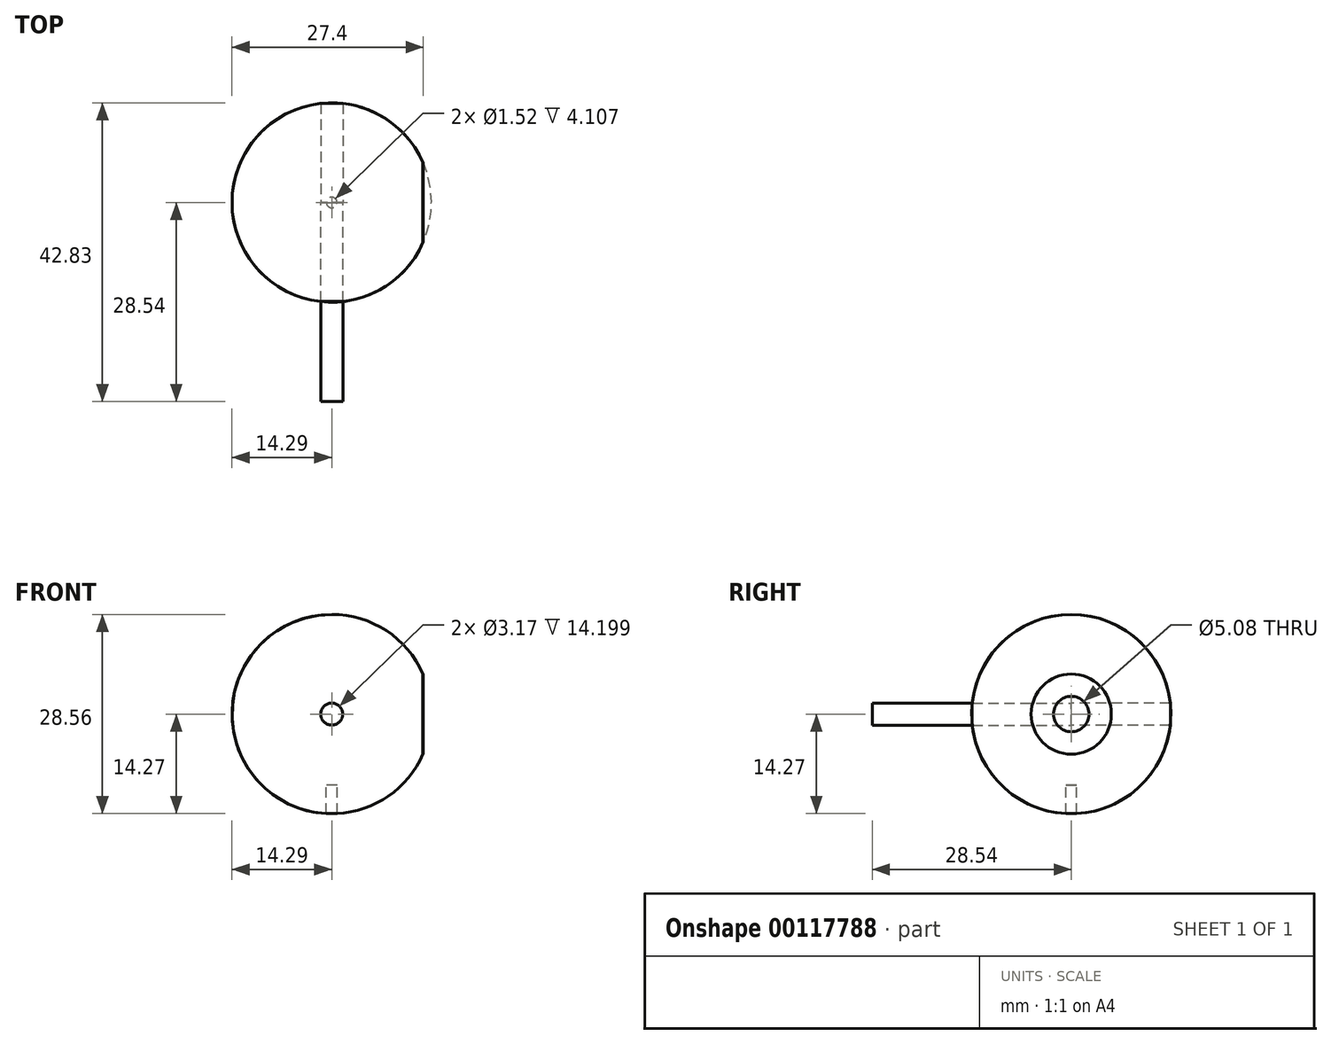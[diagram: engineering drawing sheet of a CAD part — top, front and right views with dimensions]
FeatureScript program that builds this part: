
annotation { "Feature Type Name" : "Feature", "Feature Type Description" : "" }
export const myFeature = defineFeature(function(context is Context, id is Id, definition is map)
    precondition{}
    {
        {
            var Q0;
            Q0=qCreatedBy(makeId("Front.planeOp"),FACE);
            var sketch = newSketch(context, id + "F0", { "sketchPlane" : qUnion([Q0])});
            skCircle(sketch, "E0", {"center": v(0, 0) * mm, "radius": 14.29 * mm});
            skLineSegment(sketch, "E1", {"start": v(0, 14.29) * mm, "end": v(0, -14.29) * mm});
            skSolve(sketch);
        }
        {
            var Q0;
            {var subQ0=sQuery(id+"F0.wireOp",EDGE,"E1");Q0=makeQuery(id+"F0.imprint","IMPRINT",FACE,{"disambiguationData":[TD([[makeQuery(id+"F0.imprint","IMPRINT",EDGE,{"derivedFrom":subQ0}),1.0]])]});}
            var Q1;
            Q1=sQuery(id+"F0.wireOp",EDGE,"E1");
            revolve(context, id + "F1", {"entities" : qUnion([Q0]), "axis" : qUnion([Q1]), "revolveType" : RevolveType.FULL});
        }
        {
            var Q0;
            Q0=qCreatedBy(makeId("Right.planeOp"),FACE);
            var sketch = newSketch(context, id + "F2", { "sketchPlane" : qUnion([Q0])});
            skCircle(sketch, "E2", {"center": v(0, 0) * mm, "radius": 5.78 * mm});
            skSolve(sketch);
        }
        {
            var Q0;
            Q0=makeQuery(id+"F2.imprint","IMPRINT",FACE,{"disambiguationData":[TD([[makeQuery(id+"F2.imprint","IMPRINT",EDGE,{"derivedFrom":sQuery(id+"F2.wireOp",EDGE,"Ph2NwQQo-0tcC-nFTb-9uQB-unm1SziXYBwa")}),1.0]])]});
            var Q1;
            Q1=makeQuery(id+"F2.imprint","IMPRINT",FACE,{"disambiguationData":[TD([[makeQuery(id+"F2.imprint","IMPRINT",EDGE,{"derivedFrom":sQuery(id+"F2.wireOp",EDGE,"E2")}),1.0]])]});
            var Q2;
            Q2=makeQuery(id+"F1.opRevolve","SWEPT_FACE",FACE,{"disambiguationData":[OSD([sQuery(id+"F0.wireOp",EDGE,"E0")])]});
            var Q3;
            Q3=makeQuery(id+"F1.opRevolve","SWEPT_BODY",BODY,{"disambiguationData":[OSD([sQuery(id+"F0.wireOp",EDGE,"E0"),sQuery(id+"F0.wireOp",EDGE,"E1")])]});
            var Q4;
            Q4=makeQuery(id+"F1.opRevolve","SWEPT_FACE",FACE,{"disambiguationData":[OSD([sQuery(id+"F0.wireOp",EDGE,"E0")])]});
            extrude(context, id + "F3", {"entities" : qUnion([Q0, Q1]), "operationType" : NewBodyOperationType.REMOVE, "endBound" : BoundingType.UP_TO_NEXT, "endBoundEntityFace" : qUnion([Q2]), "endBoundEntityBody" : qUnion([Q3]), "depth" : 2.54 * mm, "hasSecondDirection" : true, "secondDirectionOppositeDirection" : false, "secondDirectionBoundEntityFace" : qUnion([Q4]), "secondDirectionDepth" : 13.08 * mm});
        }
        {
            var Q0;
            Q0=makeQuery(id+"F3.boolean.opBoolean","COPY",FACE,{"derivedFrom":makeQuery(id+"F3.opExtrude","CAP_FACE",FACE,{"disambiguationData":[OSD([sQuery(id+"F2.wireOp",EDGE,"E2")])],"isStart":true})});
            var sketch = newSketch(context, id + "F4", { "sketchPlane" : qUnion([Q0])});
            skCircle(sketch, "E3", {"center": v(0, 0) * mm, "radius": 5.75 * mm});
            skCircle(sketch, "E4", {"center": v(0, 0) * mm, "radius": 2.54 * mm});
            skSolve(sketch);
        }
        {
            var Q0;
            Q0=makeQuery(id+"F4.imprint","IMPRINT",FACE,{"disambiguationData":[TD([[makeQuery(id+"F4.imprint","IMPRINT",EDGE,{"derivedFrom":sQuery(id+"F4.wireOp",EDGE,"E4")}),1.0]])]});
            extrude(context, id + "F5", {"entities" : qUnion([Q0]), "depth" : 0.03 * mm});
        }
        {
            var Q0;
            Q0=makeQuery(id+"F4.imprint","IMPRINT",FACE,{"disambiguationData":[TD([[makeQuery(id+"F4.imprint","IMPRINT",EDGE,{"derivedFrom":sQuery(id+"F4.wireOp",EDGE,"E3")}),-1.0]])]});
            extrude(context, id + "F6", {"entities" : qUnion([Q0]), "depth" : 0.03 * mm});
        }
        {
            var Q0;
            Q0=qCreatedBy(makeId("Top.planeOp"),FACE);
            var sketch = newSketch(context, id + "F7", { "sketchPlane" : qUnion([Q0])});
            skCircle(sketch, "E5", {"center": v(0, 0) * mm, "radius": 0.76 * mm});
            skSolve(sketch);
        }
        {
            var Q0;
            Q0=makeQuery(id+"F7.imprint","IMPRINT",FACE,{"disambiguationData":[TD([[makeQuery(id+"F7.imprint","IMPRINT",EDGE,{"derivedFrom":sQuery(id+"F7.wireOp",EDGE,"E5")}),1.0]])]});
            extrude(context, id + "F8", {"entities" : qUnion([Q0]), "operationType" : NewBodyOperationType.REMOVE, "oppositeDirection" : true, "depth" : 45.72 * mm, "hasSecondDirection" : true, "secondDirectionOppositeDirection" : true, "secondDirectionDepth" : 10.16 * mm, "offsetDistance" : 25.4 * mm});
        }
        {
            var Q0;
            Q0=qCreatedBy(makeId("Front.planeOp"),FACE);
            var sketch = newSketch(context, id + "F9", { "sketchPlane" : qUnion([Q0])});
            skCircle(sketch, "E6", {"center": v(0, 0) * mm, "radius": 1.59 * mm});
            skSolve(sketch);
        }
        {
            var Q0;
            Q0=makeQuery(id+"F9.imprint","IMPRINT",FACE,{"disambiguationData":[TD([[makeQuery(id+"F9.imprint","IMPRINT",EDGE,{"derivedFrom":sQuery(id+"F9.wireOp",EDGE,"E6")}),1.0]])]});
            extrude(context, id + "F10", {"entities" : qUnion([Q0]), "operationType" : NewBodyOperationType.REMOVE, "endBound" : BoundingType.UP_TO_NEXT, "depth" : 20.32 * mm});
        }
        {
            var Q0;
            Q0=makeQuery(id+"F10.boolean.opBoolean","COPY",FACE,{"derivedFrom":makeQuery(id+"F10.opExtrude","CAP_FACE",FACE,{"disambiguationData":[OSD([sQuery(id+"F9.wireOp",EDGE,"E6")])],"isStart":true})});
            extrude(context, id + "F11", {"entities" : qUnion([Q0]), "depth" : 28.54 * mm});
        }
        {
            var Q0;
            Q0=makeQuery(id+"F1.opRevolve","SWEPT_BODY",BODY,{"disambiguationData":[OSD([sQuery(id+"F0.wireOp",EDGE,"E0"),sQuery(id+"F0.wireOp",EDGE,"E1")])]});
            var Q1;
            Q1=qCreatedBy(makeId("Front.planeOp"),FACE);
            mirror(context, id + "F12", {"entities" : qUnion([Q0]), "mirrorPlane" : qUnion([Q1])});
        }
    });
